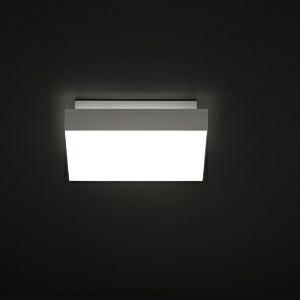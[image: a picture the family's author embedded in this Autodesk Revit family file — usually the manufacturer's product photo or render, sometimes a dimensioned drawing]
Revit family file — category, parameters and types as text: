
# Revit family: spectral_norea_norea-qa_312_2600_840_os_79bd
name_source: partatom
category: Lighting Fixtures
revit_build: Autodesk Revit 2016 (Build: 20150220_1215(x64)
units: mm (PartAtom-declared; Revit-internal decimal feet)

## family parameters
Cut with Voids When Loaded = No
Host = Face
Light Source = No
Part Type = Normal
Room Calculation Point = No
Round Connector Dimension = Use Diameter
Shared = No

## types (1)
- SPECTRAL NOREA (1 x )
    Apparent Load = 0 VA
    Approval mark = CE
    CIE Flux Codes = 48 78 95 100 58
    Control Gear = Electronic transformer
    Default Elevation = 1800 mm
    Description = SPT0000076
NOREA surface-mounted luminaire

Design:
Square luminaire element comprising an opal acrylic glass panel in a natural anodised aluminium profile frame surround. The frame is suspended at the
metal body. The LED module is formed as a square LED flat board and screwed to the luminaire element. For connection of the luminaire this can be hinged down and fastened with screws at an oblong hole in the powder-coated metal body. The indirect component is ensured by recesses in the top of the metal body. The metal body accommodates the electrical components and electronic ballast. Luminaire with heat-resistant wiring. Homogenous illumination of the light surface. Suitable for ceiling or wall mounting. 
Protection rating IP20, safety class I.

Colour:
Housing - similar to RAL 9016 white silk matt;
Frame - natural anodised
    Height = 78 mm  [stored 0.255906 ft]
    Lamp = 1 x
    Lamp count = 1
    Length = 312 mm
    Luminous efficacy = 0 lm/W
    Manufacturer = Ridi
    ModVariant = No
    Model = NOREA-QA 312/2600/840 OS
    Mounting Place = Ceiling
    Mounting Type = Surface mounted
    Number of Poles = 1
    OnlyDefault = Yes
    Power Factor = 1
    Product Name = SPECTRAL NOREA
    Product group = Ceiling mounted luminaire
    ProductGroupID = 3
    Protection Class = Protection class
    Protection Degree = IP 20
    RlxData = <blob elided: 36057 chars, md5=3f5f9706>
    Socket = socket
    Standby Power = 0 W
    System Light Flux = 0 lm
    System Power = 0 W
    Type Image = leuchtstoffklein02_-_kopie.jpg
    URL = http://reluxnet.relux.com
    VarID = 1
    Voltage = 0 V
    Weight = 0.00 kg
    Width = 312 mm

note: [stored X ft] marks values corroborated as IEEE doubles in the binary element streams (Revit-internal decimal feet)

## geometry (parser evidence)
native form markers: Sweep x11
no freeform markers — native parametric forms only
